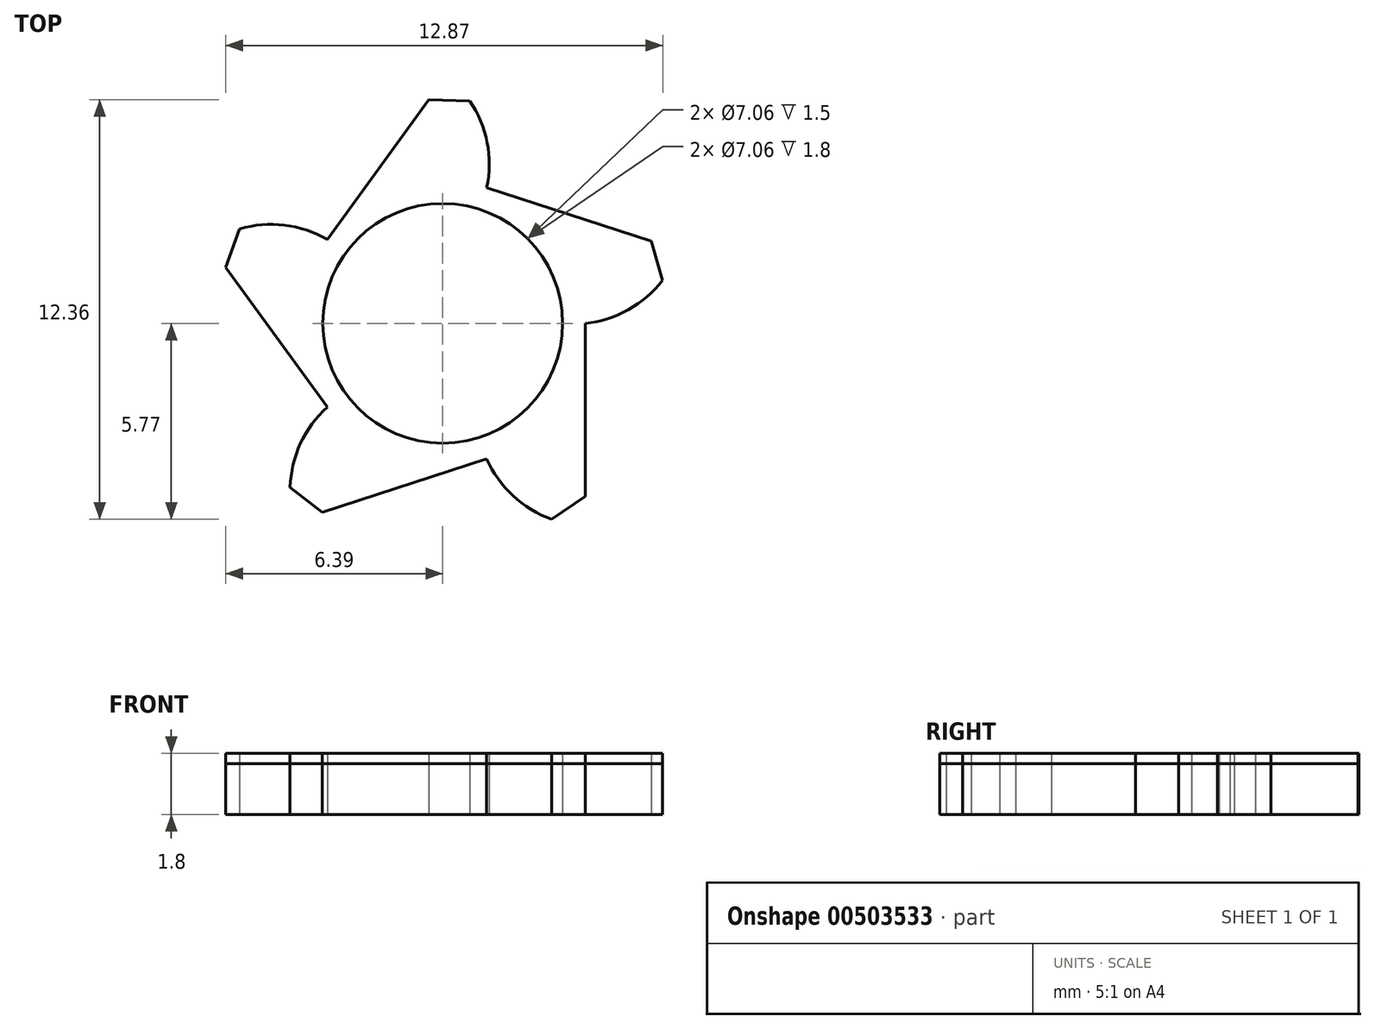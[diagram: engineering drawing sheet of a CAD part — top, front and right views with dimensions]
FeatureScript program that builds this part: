
annotation { "Feature Type Name" : "Feature", "Feature Type Description" : "" }
export const myFeature = defineFeature(function(context is Context, id is Id, definition is map)
    precondition{}
    {
        {
            var Q0;
            Q0=qCreatedBy(makeId("Top.planeOp"),FACE);
            var sketch = newSketch(context, id + "F0", { "sketchPlane" : qUnion([Q0])});
            skCircle(sketch, "E0", {"center": v(0, 0) * mm, "radius": 1.4 * mm, "construction": true});
            skCircle(sketch, "E1", {"center": v(0, 0) * mm, "radius": 1.65 * mm, "construction": true});
            skCircle(sketch, "E2", {"center": v(0, 0) * mm, "radius": 2.2 * mm, "construction": true});
            skArc(sketch, "E3", {"start": v(-1.05, -0.53) * mm, "mid": v(1.18, 0) * mm, "end": v(-1.05, 0.53) * mm});
            skLineSegment(sketch, "E4", {"start": v(0, 0) * mm, "end": v(1.4, 0) * mm, "construction": true});
            skLineSegment(sketch, "E5", {"start": v(0, 0) * mm, "end": v(0.43, -1.33) * mm, "construction": true});
            skLineSegment(sketch, "E6", {"start": v(0, 0) * mm, "end": v(-1.13, -0.82) * mm, "construction": true});
            skLineSegment(sketch, "E7", {"start": v(0, 0) * mm, "end": v(-1.13, 0.82) * mm, "construction": true});
            skLineSegment(sketch, "E8", {"start": v(0, 0) * mm, "end": v(0.43, 1.33) * mm, "construction": true});
            skLineSegment(sketch, "E9", {"start": v(1.4, 0) * mm, "end": v(1.4, -1.7) * mm});
            skLineSegment(sketch, "E10", {"start": v(1.4, -1.7) * mm, "end": v(1.07, -1.92) * mm});
            skLineSegment(sketch, "E11", {"start": v(0.43, -1.33) * mm, "end": v(-1.18, -1.86) * mm});
            skLineSegment(sketch, "E12", {"start": v(-1.18, -1.86) * mm, "end": v(-1.5, -1.61) * mm});
            skLineSegment(sketch, "E13", {"start": v(-1.13, -0.82) * mm, "end": v(-2.13, 0.55) * mm});
            skLineSegment(sketch, "E14", {"start": v(-2.13, 0.55) * mm, "end": v(-2, 0.93) * mm});
            skLineSegment(sketch, "E15", {"start": v(-1.13, 0.82) * mm, "end": v(-0.14, 2.2) * mm});
            skLineSegment(sketch, "E16", {"start": v(-0.14, 2.2) * mm, "end": v(0.26, 2.18) * mm});
            skLineSegment(sketch, "E17", {"start": v(0.43, 1.33) * mm, "end": v(2.05, 0.8) * mm});
            skLineSegment(sketch, "E18", {"start": v(2.05, 0.8) * mm, "end": v(2.16, 0.42) * mm});
            skArc(sketch, "E19", {"start": v(0.43, -1.33) * mm, "mid": v(0.7, -1.7) * mm, "end": v(1.07, -1.92) * mm});
            skPoint(sketch, "E19.third.point", {"position": v(0.36, -1.12) * mm});
            skArc(sketch, "E20", {"start": v(-1.13, -0.82) * mm, "mid": v(-1.4, -1.18) * mm, "end": v(-1.5, -1.61) * mm});
            skPoint(sketch, "E20.third.point", {"position": v(-0.95, -0.7) * mm});
            skPoint(sketch, "E21.third.point", {"position": v(-0.95, 0.7) * mm});
            skPoint(sketch, "E22.third.point", {"position": v(0.36, 1.12) * mm});
            skArc(sketch, "E23", {"start": v(1.4, 0) * mm, "mid": v(1.82, 0.13) * mm, "end": v(2.16, 0.42) * mm});
            skPoint(sketch, "E23.third.point", {"position": v(1.18, 0) * mm});
            skArc(sketch, "E24.trimOffspring", {"start": v(0.43, 1.33) * mm, "mid": v(0.44, 1.78) * mm, "end": v(0.26, 2.18) * mm});
            skLineSegment(sketch, "E25", {"start": v(0, 0) * mm, "end": v(-0.61, 0) * mm, "construction": true});
            skLineSegment(sketch, "E26", {"start": v(-0.75, 0.14) * mm, "end": v(-1.03, 0.42) * mm});
            skLineSegment(sketch, "E27", {"start": v(-0.75, -0.14) * mm, "end": v(-1.03, -0.42) * mm});
            skPoint(sketch, "E28.visualSharp", {"position": v(-0.61, 0) * mm});
            skArc(sketch, "E28.filletArc", {"start": v(-0.75, -0.14) * mm, "mid": v(-0.7, 0) * mm, "end": v(-0.75, 0.14) * mm});
            skPoint(sketch, "E29.visualSharp", {"position": v(-1.08, 0.47) * mm});
            skArc(sketch, "E29.filletArc", {"start": v(-1.05, 0.53) * mm, "mid": v(-1.06, 0.47) * mm, "end": v(-1.03, 0.42) * mm});
            skPoint(sketch, "E30.visualSharp", {"position": v(-1.08, -0.47) * mm});
            skArc(sketch, "E30.filletArc", {"start": v(-1.03, -0.42) * mm, "mid": v(-1.06, -0.47) * mm, "end": v(-1.05, -0.53) * mm});
            skLineSegment(sketch, "E31", {"start": v(0, 0) * mm, "end": v(-2.17, 0.34) * mm, "construction": true});
            skArc(sketch, "E32", {"start": v(-1.13, 0.82) * mm, "mid": v(-1.55, 0.96) * mm, "end": v(-2, 0.93) * mm});
            skArc(sketch, "E33", {"start": v(-1.05, 0.53) * mm, "mid": v(-1.18, 0) * mm, "end": v(-1.05, -0.53) * mm});
            skSolve(sketch);
        }
        {
            var Q0;
            Q0=makeQuery(id+"F0.imprint","IMPRINT",FACE,{"disambiguationData":[TD([[makeQuery(id+"F0.imprint","IMPRINT",EDGE,{"derivedFrom":sQuery(id+"F0.wireOp",EDGE,"E3")}),-1.0]])]});
            extrude(context, id + "F1", {"entities" : qUnion([Q0]), "depth" : 0.5 * mm});
        }
        {
            var Q0;
            Q0=makeQuery(id+"F0.imprint","IMPRINT",FACE,{"disambiguationData":[TD([[makeQuery(id+"F0.imprint","IMPRINT",EDGE,{"derivedFrom":sQuery(id+"F0.wireOp",EDGE,"E3")}),-1.0]])]});
            extrude(context, id + "F2", {"entities" : qUnion([Q0]), "depth" : 0.6 * mm});
        }
        {
            var Q0;
            Q0=makeQuery(id+"F2.opExtrude","SWEPT_BODY",BODY,{"disambiguationData":[OSD([sQuery(id+"F0.wireOp",EDGE,"E3"),sQuery(id+"F0.wireOp",EDGE,"E9"),sQuery(id+"F0.wireOp",EDGE,"E10"),sQuery(id+"F0.wireOp",EDGE,"E11"),sQuery(id+"F0.wireOp",EDGE,"E12"),sQuery(id+"F0.wireOp",EDGE,"E13"),sQuery(id+"F0.wireOp",EDGE,"E14"),sQuery(id+"F0.wireOp",EDGE,"E15"),sQuery(id+"F0.wireOp",EDGE,"E16"),sQuery(id+"F0.wireOp",EDGE,"E17"),sQuery(id+"F0.wireOp",EDGE,"E18"),sQuery(id+"F0.wireOp",EDGE,"E19"),sQuery(id+"F0.wireOp",EDGE,"E20"),sQuery(id+"F0.wireOp",EDGE,"E23"),sQuery(id+"F0.wireOp",EDGE,"E24.trimOffspring"),sQuery(id+"F0.wireOp",EDGE,"E26"),sQuery(id+"F0.wireOp",EDGE,"E27"),sQuery(id+"F0.wireOp",EDGE,"E28.filletArc"),sQuery(id+"F0.wireOp",EDGE,"E29.filletArc"),sQuery(id+"F0.wireOp",EDGE,"E30.filletArc"),sQuery(id+"F0.wireOp",EDGE,"E32")])]});
            var Q1;
            Q1=makeQuery(id+"F1.opExtrude","SWEPT_BODY",BODY,{"disambiguationData":[OSD([sQuery(id+"F0.wireOp",EDGE,"E3"),sQuery(id+"F0.wireOp",EDGE,"E9"),sQuery(id+"F0.wireOp",EDGE,"E10"),sQuery(id+"F0.wireOp",EDGE,"E11"),sQuery(id+"F0.wireOp",EDGE,"E12"),sQuery(id+"F0.wireOp",EDGE,"E13"),sQuery(id+"F0.wireOp",EDGE,"E14"),sQuery(id+"F0.wireOp",EDGE,"E15"),sQuery(id+"F0.wireOp",EDGE,"E16"),sQuery(id+"F0.wireOp",EDGE,"E17"),sQuery(id+"F0.wireOp",EDGE,"E18"),sQuery(id+"F0.wireOp",EDGE,"E19"),sQuery(id+"F0.wireOp",EDGE,"E20"),sQuery(id+"F0.wireOp",EDGE,"E23"),sQuery(id+"F0.wireOp",EDGE,"E24.trimOffspring"),sQuery(id+"F0.wireOp",EDGE,"E26"),sQuery(id+"F0.wireOp",EDGE,"E27"),sQuery(id+"F0.wireOp",EDGE,"E28.filletArc"),sQuery(id+"F0.wireOp",EDGE,"E29.filletArc"),sQuery(id+"F0.wireOp",EDGE,"E30.filletArc"),sQuery(id+"F0.wireOp",EDGE,"E32")])]});
            var Q2;
            Q2=qCreatedBy(makeId("Origin.pointOp"),VERTEX);
            transform(context, id + "F3", {"entities" : qUnion([Q0, Q1]), "transformType" : TransformType.SCALE_UNIFORMLY, "scale" : 3, "makeCopy" : false, "scalePoint" : qUnion([Q2])});
        }
    });
